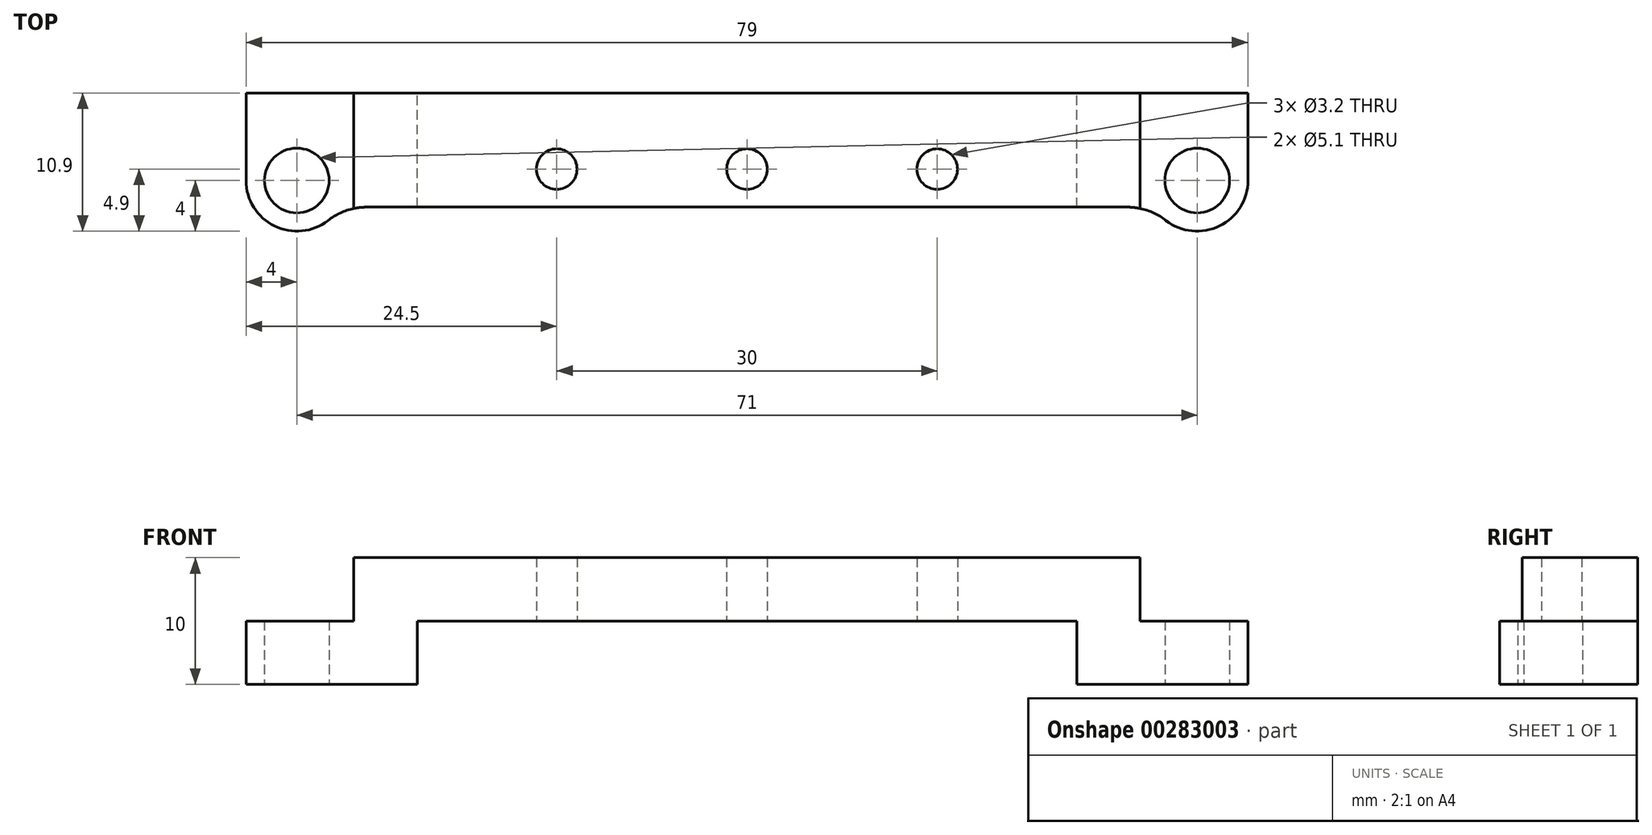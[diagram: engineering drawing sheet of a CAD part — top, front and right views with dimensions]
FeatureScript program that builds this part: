
annotation { "Feature Type Name" : "Feature", "Feature Type Description" : "" }
export const myFeature = defineFeature(function(context is Context, id is Id, definition is map)
    precondition{}
    {
        {
            var Q0;
            Q0=qCreatedBy(makeId("Front.planeOp"),FACE);
            var sketch = newSketch(context, id + "F0", { "sketchPlane" : qUnion([Q0])});
            skLineSegment(sketch, "E0", {"start": v(0, 0) * mm, "end": v(-26, 0) * mm});
            skLineSegment(sketch, "E1", {"start": v(-26, 0) * mm, "end": v(-26, -5) * mm});
            skLineSegment(sketch, "E2", {"start": v(-26, -5) * mm, "end": v(-39.5, -5) * mm});
            skLineSegment(sketch, "E3", {"start": v(-39.5, -5) * mm, "end": v(-39.5, 0) * mm});
            skLineSegment(sketch, "E4", {"start": v(-39.5, 0) * mm, "end": v(-31, 0) * mm});
            skLineSegment(sketch, "E5", {"start": v(-31, 0) * mm, "end": v(-31, 5) * mm});
            skLineSegment(sketch, "E6", {"start": v(-31, 5) * mm, "end": v(0, 5) * mm});
            skLineSegment(sketch, "E7", {"start": v(0, 5) * mm, "end": v(0, 0) * mm});
            skSolve(sketch);
        }
        {
            var Q0;
            Q0=makeQuery(id+"F0.imprint","IMPRINT",FACE,{"disambiguationData":[TD([[makeQuery(id+"F0.imprint","IMPRINT",EDGE,{"derivedFrom":sQuery(id+"F0.wireOp",EDGE,"E0")}),-1.0]])]});
            extrude(context, id + "F1", {"entities" : qUnion([Q0]), "depth" : 10.9 * mm});
        }
        {
            var Q0;
            Q0=makeQuery(id+"F1.opExtrude","SWEPT_FACE",FACE,{"disambiguationData":[OSD([sQuery(id+"F0.wireOp",EDGE,"E2")])]});
            var sketch = newSketch(context, id + "F2", { "sketchPlane" : qUnion([Q0])});
            skArc(sketch, "E8", {"start": v(-32.1, 9) * mm, "mid": v(-36.6, 10.75) * mm, "end": v(-39.5, 6.9) * mm});
            skLineSegment(sketch, "E9", {"start": v(0, 9) * mm, "end": v(-32.1, 9) * mm});
            skLineSegment(sketch, "E10", {"start": v(-39.5, 6.9) * mm, "end": v(-39.5, 12.9) * mm});
            skLineSegment(sketch, "E11", {"start": v(-39.5, 12.9) * mm, "end": v(0, 12.9) * mm});
            skLineSegment(sketch, "E12", {"start": v(0, 12.9) * mm, "end": v(0, 9) * mm});
            skSolve(sketch);
        }
        {
            var Q0;
            Q0=qSketchRegion(id+"F2",true);
            var Q1;
            Q1=makeQuery(id+"F1.opExtrude","SWEPT_FACE",FACE,{"disambiguationData":[OSD([sQuery(id+"F0.wireOp",EDGE,"E6")])]});
            extrude(context, id + "F3", {"entities" : qUnion([Q0]), "operationType" : NewBodyOperationType.REMOVE, "endBound" : BoundingType.UP_TO_SURFACE, "oppositeDirection" : true, "endBoundEntityFace" : qUnion([Q1]), "depth" : 25 * mm});
        }
        {
            var Q0;
            Q0=makeQuery(id+"F3.boolean.opBoolean","COPY",EDGE,{"derivedFrom":makeQuery(id+"F3.opExtrude","SWEPT_EDGE",EDGE,{"disambiguationData":[OSD([sQuery(id+"F2.wireOp",EDGE,"E8"),sQuery(id+"F2.wireOp",EDGE,"E9")])]})});
            fillet(context, id + "F4", {"entities" : qUnion([Q0]), "radius" : 5 * mm, "tangentPropagation" : true, "allowEdgeOverflow" : false});
        }
        {
            var Q0;
            Q0=makeQuery(id+"F1.opExtrude","SWEPT_FACE",FACE,{"disambiguationData":[OSD([sQuery(id+"F0.wireOp",EDGE,"E2")])]});
            var sketch = newSketch(context, id + "F5", { "sketchPlane" : qUnion([Q0])});
            skArc(sketch, "E13.0", {"start": v(-33.04, 10.06) * mm, "mid": v(-37.26, 10.5) * mm, "end": v(-39.5, 6.9) * mm});
            skSolve(sketch);
        }
        {
            var Q0;
            Q0=sQuery(id+"F5.wireOp",VERTEX,"E13.0.center");
            var Q1;
            Q1=makeQuery(id+"F1.opExtrude","SWEPT_BODY",BODY,{"disambiguationData":[OSD([sQuery(id+"F0.wireOp",EDGE,"E0"),sQuery(id+"F0.wireOp",EDGE,"E1"),sQuery(id+"F0.wireOp",EDGE,"E2"),sQuery(id+"F0.wireOp",EDGE,"E3"),sQuery(id+"F0.wireOp",EDGE,"E4"),sQuery(id+"F0.wireOp",EDGE,"E5"),sQuery(id+"F0.wireOp",EDGE,"E6"),sQuery(id+"F0.wireOp",EDGE,"E7")])]});
            hole(context, id + "F6", {"style" : HoleStyle.SIMPLE, "endStyle" : HoleEndStyle.THROUGH, "holeDiameter" : 5.1 * mm, "tappedDepth" : 12 * mm, "tapClearance" : 3, "locations" : qUnion([Q0]), "scope" : qUnion([Q1])});
        }
        {
            var Q0;
            Q0=makeQuery(id+"F1.opExtrude","SWEPT_BODY",BODY,{"disambiguationData":[OSD([sQuery(id+"F0.wireOp",EDGE,"E0"),sQuery(id+"F0.wireOp",EDGE,"E1"),sQuery(id+"F0.wireOp",EDGE,"E2"),sQuery(id+"F0.wireOp",EDGE,"E3"),sQuery(id+"F0.wireOp",EDGE,"E4"),sQuery(id+"F0.wireOp",EDGE,"E5"),sQuery(id+"F0.wireOp",EDGE,"E6"),sQuery(id+"F0.wireOp",EDGE,"E7")])]});
            var Q1;
            Q1=makeQuery(id+"F1.opExtrude","SWEPT_FACE",FACE,{"disambiguationData":[OSD([sQuery(id+"F0.wireOp",EDGE,"E7")])]});
            mirror(context, id + "F7", {"operationType" : NewBodyOperationType.ADD, "entities" : qUnion([Q0]), "mirrorPlane" : qUnion([Q1])});
        }
        {
            var Q0;
            Q0=qCreatedBy(makeId("Top.planeOp"),FACE);
            var sketch = newSketch(context, id + "F8", { "sketchPlane" : qUnion([Q0])});
            skLineSegment(sketch, "E14.0.0", {"start": v(-26, 0) * mm, "end": v(26, 0) * mm, "construction": true});
            skLineSegment(sketch, "E14.0.1", {"start": v(26, 0) * mm, "end": v(26, -9) * mm, "construction": true});
            skLineSegment(sketch, "E14.0.2", {"start": v(26, -9) * mm, "end": v(-26, -9) * mm, "construction": true});
            skLineSegment(sketch, "E14.0.3", {"start": v(-26, -9) * mm, "end": v(-26, 0) * mm, "construction": true});
            skPoint(sketch, "E15", {"position": v(0, -6) * mm});
            skPoint(sketch, "E16", {"position": v(15, -6) * mm});
            skPoint(sketch, "E17", {"position": v(-15, -6) * mm});
            skSolve(sketch);
        }
        {
            var Q0;
            Q0=sQuery(id+"F8.wireOp",VERTEX,"E17");
            var Q1;
            Q1=sQuery(id+"F8.wireOp",VERTEX,"E15");
            var Q2;
            Q2=sQuery(id+"F8.wireOp",VERTEX,"E16");
            var Q3;
            Q3=makeQuery(id+"F1.opExtrude","SWEPT_BODY",BODY,{"disambiguationData":[OSD([sQuery(id+"F0.wireOp",EDGE,"E0"),sQuery(id+"F0.wireOp",EDGE,"E1"),sQuery(id+"F0.wireOp",EDGE,"E2"),sQuery(id+"F0.wireOp",EDGE,"E3"),sQuery(id+"F0.wireOp",EDGE,"E4"),sQuery(id+"F0.wireOp",EDGE,"E5"),sQuery(id+"F0.wireOp",EDGE,"E6"),sQuery(id+"F0.wireOp",EDGE,"E7")])]});
            hole(context, id + "F9", {"style" : HoleStyle.SIMPLE, "endStyle" : HoleEndStyle.THROUGH, "oppositeDirection" : true, "standardTappedOrClearance" : lookupTablePath({ "standard" : "ISO", "engagement" : "75%", "pitch" : "0.75 mm", "size" : "M4", "type" : "Tapped" }), "standardBlindInLast" : lookupTablePath({ "standard" : "ISO", "engagement" : "75%", "pitch" : "0.75 mm", "size" : "M4", "type" : "Tapped" }), "holeDiameter" : 3.2 * mm, "showTappedDepth" : true, "tappedDepth" : 12 * mm, "tapClearance" : 3, "locations" : qUnion([Q0, Q1, Q2]), "scope" : qUnion([Q3])});
        }
    });
